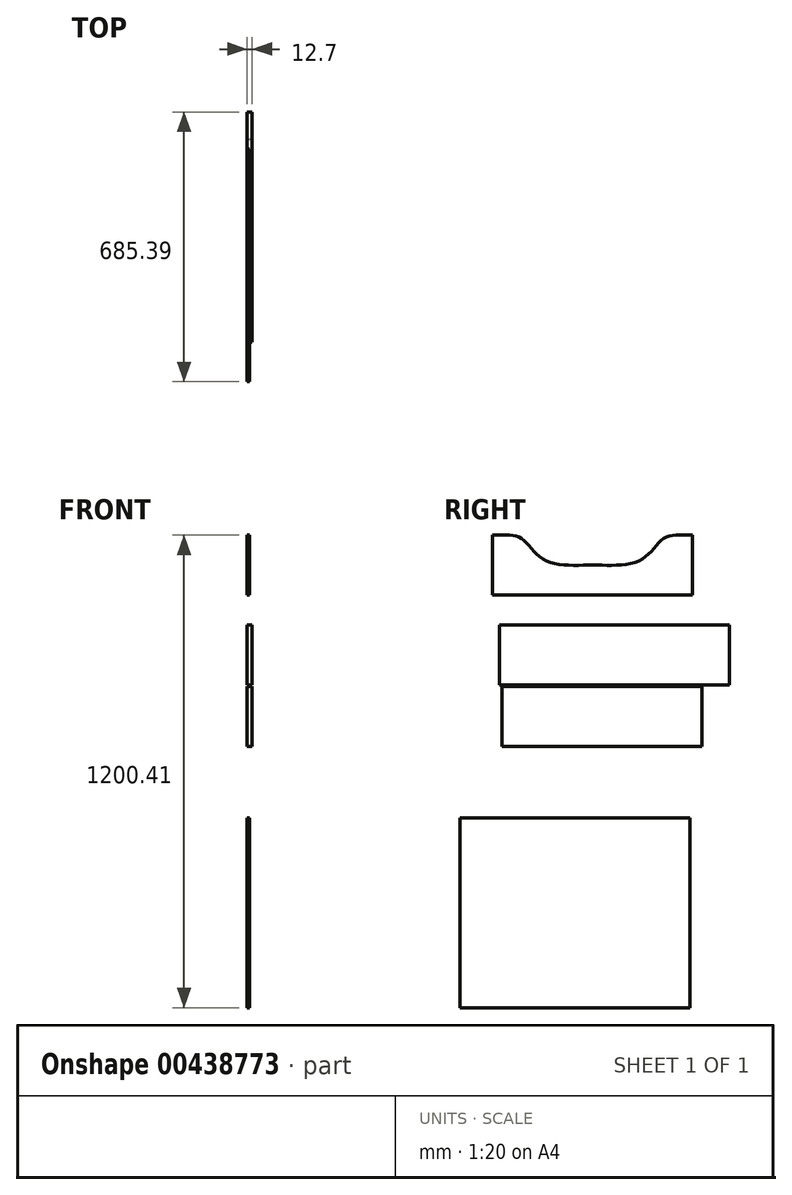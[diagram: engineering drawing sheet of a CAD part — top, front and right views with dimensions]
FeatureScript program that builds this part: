
annotation { "Feature Type Name" : "Feature", "Feature Type Description" : "" }
export const myFeature = defineFeature(function(context is Context, id is Id, definition is map)
    precondition{}
    {
        {
            var Q0;
            Q0=qCreatedBy(makeId("Right.planeOp"),FACE);
            var sketch = newSketch(context, id + "F0", { "sketchPlane" : qUnion([Q0])});
            skLineSegment(sketch, "E0.bottom", {"start": v(292.1, 76.2) * mm, "end": v(-292.1, 76.2) * mm});
            skLineSegment(sketch, "E0.top", {"start": v(292.1, -76.2) * mm, "end": v(-292.1, -76.2) * mm});
            skLineSegment(sketch, "E0.left", {"start": v(292.1, 76.2) * mm, "end": v(292.1, -76.2) * mm});
            skLineSegment(sketch, "E0.right", {"start": v(-292.1, 76.2) * mm, "end": v(-292.1, -76.2) * mm});
            skPoint(sketch, "E0.middle", {"position": v(0, 0) * mm});
            skSolve(sketch);
        }
        {
            var Q0;
            Q0=makeQuery(id+"F0.imprint","IMPRINT",FACE,{"disambiguationData":[TD([[makeQuery(id+"F0.imprint","IMPRINT",EDGE,{"derivedFrom":sQuery(id+"F0.wireOp",EDGE,"E0.bottom")}),1.0]])]});
            extrude(context, id + "F1", {"entities" : qUnion([Q0]), "depth" : 12.7 * mm});
        }
        {
            var Q0;
            Q0=qCreatedBy(makeId("Right.planeOp"),FACE);
            var sketch = newSketch(context, id + "F2", { "sketchPlane" : qUnion([Q0])});
            skLineSegment(sketch, "E1.bottom", {"start": v(-285.62, -80.14) * mm, "end": v(222.38, -80.14) * mm});
            skLineSegment(sketch, "E1.top", {"start": v(-285.62, -232.54) * mm, "end": v(222.38, -232.54) * mm});
            skLineSegment(sketch, "E1.left", {"start": v(-285.62, -80.14) * mm, "end": v(-285.62, -232.54) * mm});
            skLineSegment(sketch, "E1.right", {"start": v(222.38, -80.14) * mm, "end": v(222.38, -232.54) * mm});
            skSolve(sketch);
        }
        {
            var Q0;
            Q0=makeQuery(id+"F2.imprint","IMPRINT",FACE,{"disambiguationData":[TD([[makeQuery(id+"F2.imprint","IMPRINT",EDGE,{"derivedFrom":sQuery(id+"F2.wireOp",EDGE,"E1.bottom")}),-1.0]])]});
            extrude(context, id + "F3", {"entities" : qUnion([Q0]), "depth" : 12.7 * mm});
        }
        {
            var Q0;
            Q0=qCreatedBy(makeId("Right.planeOp"),FACE);
            var sketch = newSketch(context, id + "F4", { "sketchPlane" : qUnion([Q0])});
            skLineSegment(sketch, "E2.bottom", {"start": v(-393.29, -413.2) * mm, "end": v(190.91, -413.2) * mm});
            skLineSegment(sketch, "E2.top", {"start": v(-393.29, -895.8) * mm, "end": v(190.91, -895.8) * mm});
            skLineSegment(sketch, "E2.left", {"start": v(-393.29, -413.2) * mm, "end": v(-393.29, -895.8) * mm});
            skLineSegment(sketch, "E2.right", {"start": v(190.91, -413.2) * mm, "end": v(190.91, -895.8) * mm});
            skSolve(sketch);
        }
        {
            var Q0;
            Q0=makeQuery(id+"F4.imprint","IMPRINT",FACE,{"disambiguationData":[TD([[makeQuery(id+"F4.imprint","IMPRINT",EDGE,{"derivedFrom":sQuery(id+"F4.wireOp",EDGE,"E2.bottom")}),-1.0]])]});
            extrude(context, id + "F5", {"entities" : qUnion([Q0]), "depth" : 6.35 * mm});
        }
        {
            var Q0;
            Q0=qCreatedBy(makeId("Right.planeOp"),FACE);
            var sketch = newSketch(context, id + "F6", { "sketchPlane" : qUnion([Q0])});
            skLineSegment(sketch, "E3.bottom", {"start": v(-309.86, 152.22) * mm, "end": v(198.14, 152.22) * mm});
            skLineSegment(sketch, "E3.top", {"start": v(-309.86, 304.62) * mm, "end": v(198.14, 304.62) * mm});
            skLineSegment(sketch, "E3.left", {"start": v(-309.86, 152.22) * mm, "end": v(-309.86, 304.62) * mm});
            skLineSegment(sketch, "E3.right", {"start": v(198.14, 152.22) * mm, "end": v(198.14, 304.62) * mm});
            skLineSegment(sketch, "E4", {"start": v(-55.86, 304.62) * mm, "end": v(-55.86, 228.42) * mm});
            skFitSpline(sketch, "E5", {"points": [v(-55.86, 228.42) * mm, v(66.35, 241.53) * mm, v(124.24, 295.68) * mm, v(198.14, 304.62) * mm], "startDerivative": vector(307.56, 4.43) * mm, "endDerivative": vector(327.32, -0.87) * mm});
            skFitSpline(sketch, "E6.MirrorCS", {"points": [v(-55.86, 228.42) * mm, v(-178.07, 241.53) * mm, v(-235.95, 295.68) * mm, v(-309.86, 304.62) * mm], "startDerivative": vector(-307.56, 4.43) * mm, "endDerivative": vector(-327.32, -0.87) * mm});
            skSolve(sketch);
        }
        {
            var Q0;
            Q0=makeQuery(id+"F6.imprint","IMPRINT",FACE,{"disambiguationData":[TD([[makeQuery(id+"F6.imprint","IMPRINT",EDGE,{"derivedFrom":sQuery(id+"F6.wireOp",EDGE,"E3.bottom")}),1.0]])]});
            extrude(context, id + "F7", {"entities" : qUnion([Q0]), "depth" : 6.35 * mm});
        }
    });
